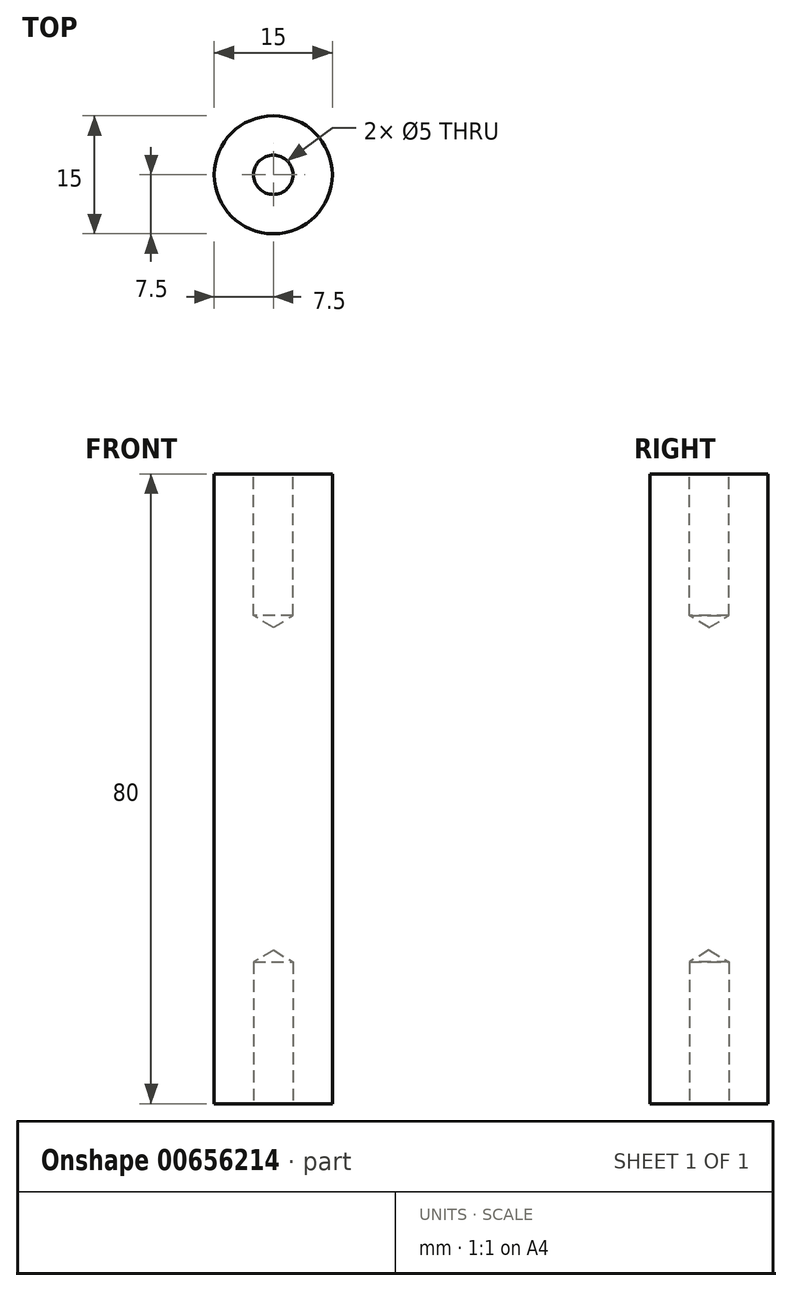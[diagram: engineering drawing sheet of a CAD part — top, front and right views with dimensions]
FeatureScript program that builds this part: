
annotation { "Feature Type Name" : "Feature", "Feature Type Description" : "" }
export const myFeature = defineFeature(function(context is Context, id is Id, definition is map)
    precondition{}
    {
        {
            var Q0;
            Q0=qCreatedBy(makeId("Front.planeOp"),FACE);
            var sketch = newSketch(context, id + "F0", { "sketchPlane" : qUnion([Q0])});
            skLineSegment(sketch, "E0", {"start": v(2, 80) * mm, "end": v(7.5, 80) * mm});
            skLineSegment(sketch, "E1", {"start": v(7.5, 80) * mm, "end": v(7.5, 0) * mm});
            skLineSegment(sketch, "E2", {"start": v(7.5, 0) * mm, "end": v(2, 0) * mm});
            skLineSegment(sketch, "E3", {"start": v(2, 80) * mm, "end": v(2, 65) * mm});
            skLineSegment(sketch, "E4", {"start": v(2, 65) * mm, "end": v(0, 65) * mm});
            skLineSegment(sketch, "E5", {"start": v(2, 0) * mm, "end": v(2, 15) * mm});
            skLineSegment(sketch, "E6", {"start": v(2, 15) * mm, "end": v(0, 15) * mm});
            skPoint(sketch, "E7.orphan", {"position": v(0, 0) * mm});
            skLineSegment(sketch, "E8", {"start": v(0, 0) * mm, "end": v(0, 97.12) * mm, "construction": true});
            skLineSegment(sketch, "E9", {"start": v(0, 65) * mm, "end": v(0, 15) * mm});
            skSolve(sketch);
        }
        {
            var Q0;
            Q0=qSketchRegion(id+"F0",true);
            var Q1;
            Q1=sQuery(id+"F0.wireOp",EDGE,"E8");
            revolve(context, id + "F1", {"entities" : qUnion([Q0]), "axis" : qUnion([Q1]), "revolveType" : RevolveType.FULL});
        }
        {
            var Q0;
            Q0=makeQuery(id+"F1.opRevolve","SWEPT_FACE",FACE,{"disambiguationData":[OSD([sQuery(id+"F0.wireOp",EDGE,"E0")])]});
            var sketch = newSketch(context, id + "F2", { "sketchPlane" : qUnion([Q0])});
            skCircle(sketch, "E10", {"center": v(0, 0) * mm, "radius": 3 * mm});
            skSolve(sketch);
        }
        {
            var Q0;
            Q0=sQuery(id+"F2.wireOp",VERTEX,"E10.center");
            var Q1;
            Q1=makeQuery(id+"F1.opRevolve","SWEPT_BODY",BODY,{"disambiguationData":[OSD([sQuery(id+"F0.wireOp",EDGE,"E0"),sQuery(id+"F0.wireOp",EDGE,"E1"),sQuery(id+"F0.wireOp",EDGE,"E2"),sQuery(id+"F0.wireOp",EDGE,"E3"),sQuery(id+"F0.wireOp",EDGE,"E4"),sQuery(id+"F0.wireOp",EDGE,"E5"),sQuery(id+"F0.wireOp",EDGE,"E6"),sQuery(id+"F0.wireOp",EDGE,"E9")])]});
            hole(context, id + "F3", {"style" : HoleStyle.SIMPLE, "endStyle" : HoleEndStyle.BLIND, "standardTappedOrClearance" : lookupTablePath({ "standard" : "ISO", "engagement" : "75%", "pitch" : "1 mm", "size" : "M6", "type" : "Tapped" }), "standardBlindInLast" : lookupTablePath({ "standard" : "ISO", "engagement" : "75%", "pitch" : "1 mm", "size" : "M6", "type" : "Tapped" }), "holeDiameter" : 5 * mm, "majorDiameter" : 6 * mm, "showTappedDepth" : true, "holeDepth" : 18 * mm, "isTappedThrough" : true, "tappedDepth" : 15 * mm, "tapClearance" : 3, "locations" : qUnion([Q0]), "scope" : qUnion([Q1])});
        }
        {
            var Q0;
            Q0=makeQuery(id+"F1.opRevolve","SWEPT_FACE",FACE,{"disambiguationData":[OSD([sQuery(id+"F0.wireOp",EDGE,"E2")])]});
            var sketch = newSketch(context, id + "F4", { "sketchPlane" : qUnion([Q0])});
            skCircle(sketch, "E11", {"center": v(0, 0) * mm, "radius": 2.74 * mm});
            skSolve(sketch);
        }
        {
            var Q0;
            Q0=sQuery(id+"F4.wireOp",VERTEX,"E11.center");
            var Q1;
            Q1=makeQuery(id+"F1.opRevolve","SWEPT_BODY",BODY,{"disambiguationData":[OSD([sQuery(id+"F0.wireOp",EDGE,"E0"),sQuery(id+"F0.wireOp",EDGE,"E1"),sQuery(id+"F0.wireOp",EDGE,"E2"),sQuery(id+"F0.wireOp",EDGE,"E3"),sQuery(id+"F0.wireOp",EDGE,"E4"),sQuery(id+"F0.wireOp",EDGE,"E5"),sQuery(id+"F0.wireOp",EDGE,"E6"),sQuery(id+"F0.wireOp",EDGE,"E9")])]});
            hole(context, id + "F5", {"style" : HoleStyle.SIMPLE, "endStyle" : HoleEndStyle.BLIND, "standardTappedOrClearance" : lookupTablePath({ "standard" : "ISO", "engagement" : "75%", "pitch" : "1 mm", "size" : "M6", "type" : "Tapped" }), "standardBlindInLast" : lookupTablePath({ "standard" : "ISO", "engagement" : "75%", "pitch" : "1 mm", "size" : "M6", "type" : "Tapped" }), "holeDiameter" : 5 * mm, "majorDiameter" : 6 * mm, "showTappedDepth" : true, "holeDepth" : 18 * mm, "isTappedThrough" : true, "tappedDepth" : 15 * mm, "tapClearance" : 3, "locations" : qUnion([Q0]), "scope" : qUnion([Q1])});
        }
    });
